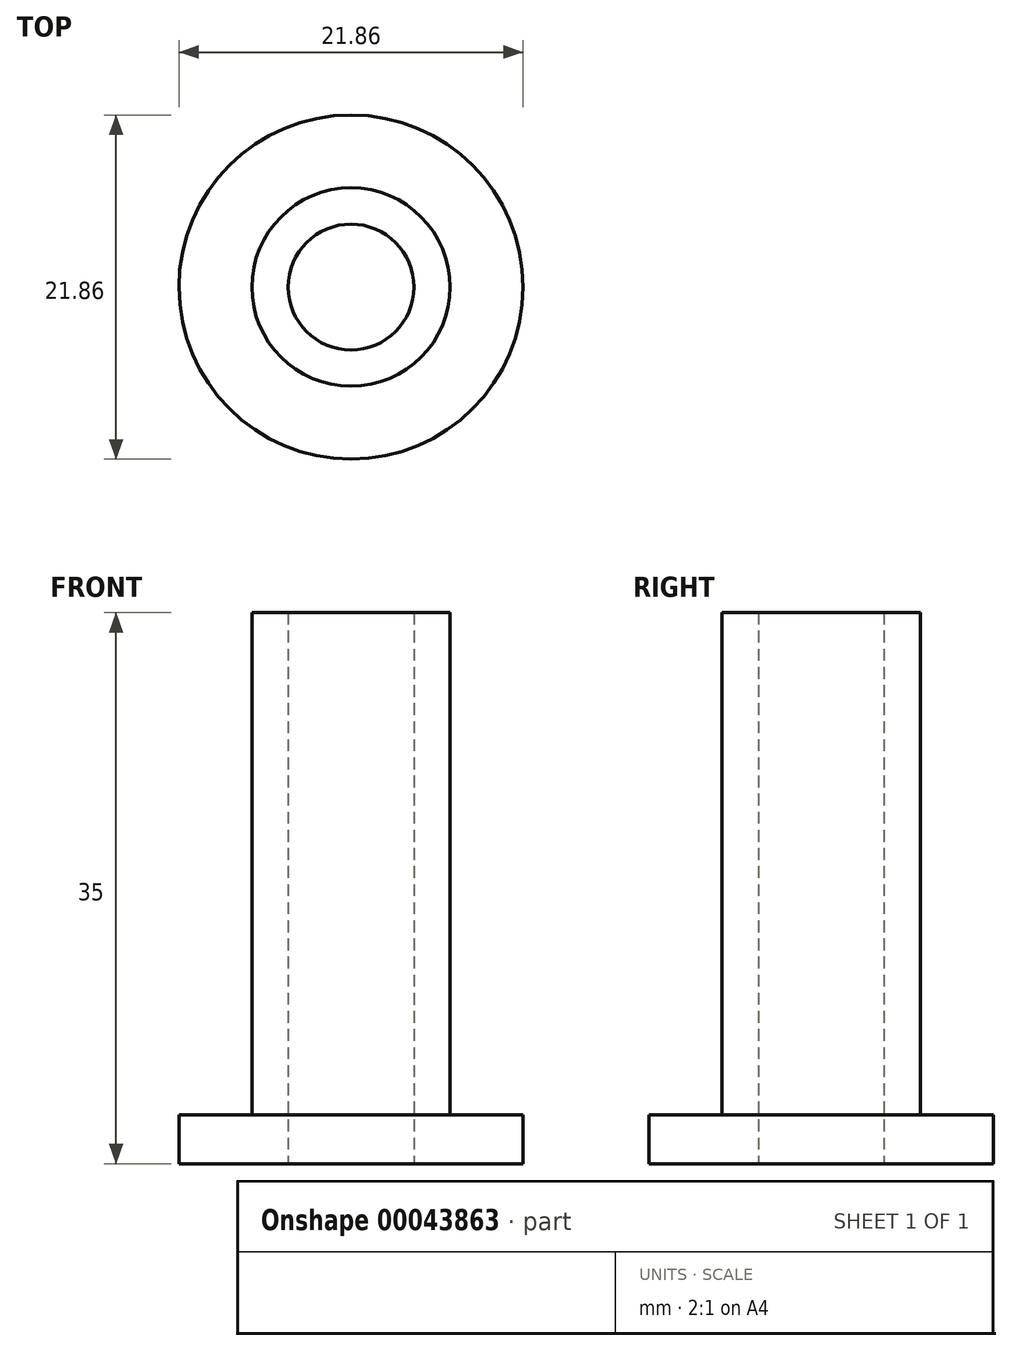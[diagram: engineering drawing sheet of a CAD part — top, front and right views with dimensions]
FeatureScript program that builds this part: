
annotation { "Feature Type Name" : "Feature", "Feature Type Description" : "" }
export const myFeature = defineFeature(function(context is Context, id is Id, definition is map)
    precondition{}
    {
        {
            var Q0;
            Q0=qCreatedBy(makeId("Top.planeOp"),FACE);
            var sketch = newSketch(context, id + "F0", { "sketchPlane" : qUnion([Q0])});
            skCircle(sketch, "E0", {"center": v(0, 0) * mm, "radius": 10.93 * mm});
            skCircle(sketch, "E1", {"center": v(0, 0) * mm, "radius": 4 * mm});
            skSolve(sketch);
        }
        {
            var Q0;
            Q0=makeQuery(id+"F0.imprint","IMPRINT",FACE,{"disambiguationData":[TD([[makeQuery(id+"F0.imprint","IMPRINT",EDGE,{"derivedFrom":sQuery(id+"F0.wireOp",EDGE,"E0")}),1.0]])]});
            extrude(context, id + "F1", {"entities" : qUnion([Q0]), "depth" : 3.1 * mm, "offsetDistance" : 25 * mm});
        }
        {
            var Q0;
            Q0=makeQuery(id+"F1.opExtrude","CAP_FACE",FACE,{"disambiguationData":[OSD([sQuery(id+"F0.wireOp",EDGE,"E0"),sQuery(id+"F0.wireOp",EDGE,"E1")])],"isStart":false});
            var sketch = newSketch(context, id + "F2", { "sketchPlane" : qUnion([Q0])});
            skCircle(sketch, "E2", {"center": v(0, 0) * mm, "radius": 6.3 * mm});
            skSolve(sketch);
        }
        {
            var Q0;
            Q0=makeQuery(id+"F2.imprint","IMPRINT",FACE,{"disambiguationData":[TD([[makeQuery(id+"F2.imprint","IMPRINT",EDGE,{"derivedFrom":sQuery(id+"F2.wireOp",EDGE,"E2")}),1.0]])]});
            extrude(context, id + "F3", {"entities" : qUnion([Q0]), "operationType" : NewBodyOperationType.ADD, "depth" : 31.9 * mm, "offsetDistance" : 25 * mm});
        }
    });
